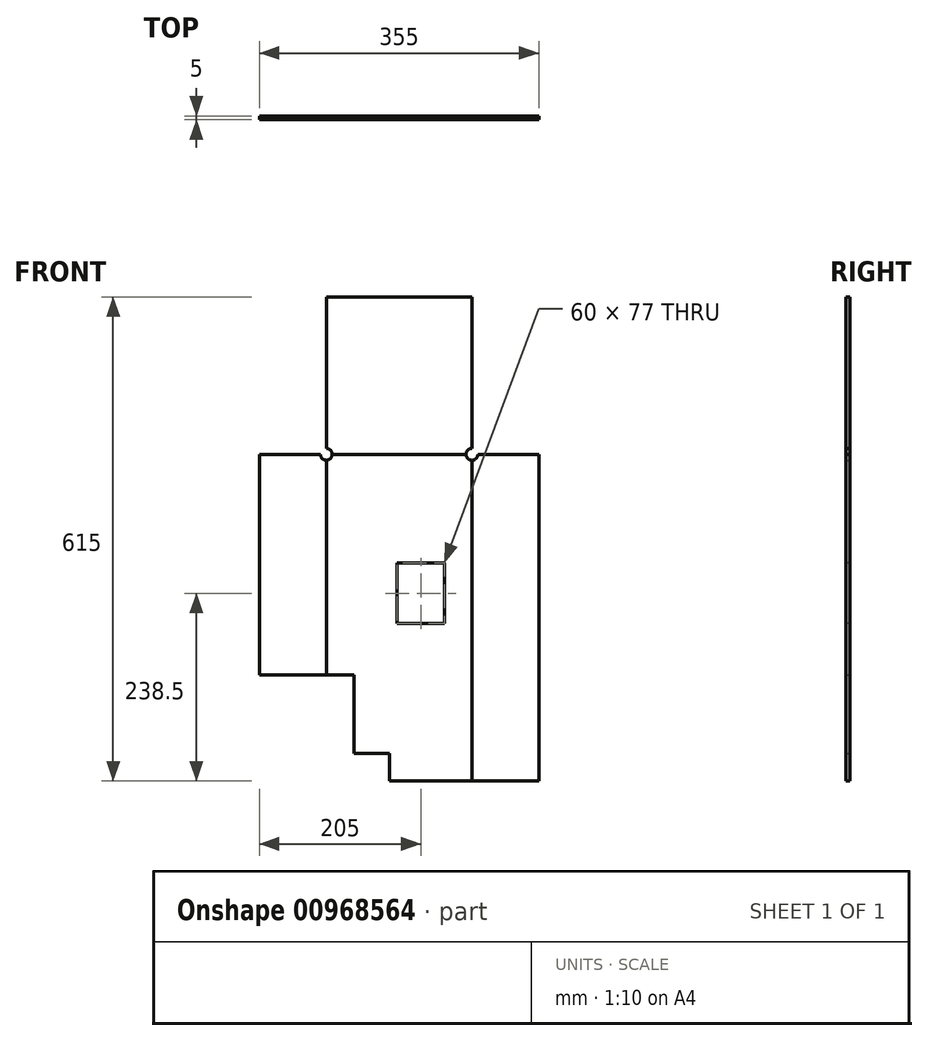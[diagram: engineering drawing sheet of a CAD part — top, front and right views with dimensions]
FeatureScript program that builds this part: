
annotation { "Feature Type Name" : "Feature", "Feature Type Description" : "" }
export const myFeature = defineFeature(function(context is Context, id is Id, definition is map)
    precondition{}
    {
        {
            var Q0;
            Q0=qCreatedBy(makeId("Front.planeOp"),FACE);
            var sketch = newSketch(context, id + "F0", { "sketchPlane" : qUnion([Q0])});
            skLineSegment(sketch, "E0.bottom", {"start": v(7.5, 0) * mm, "end": v(177.5, 0) * mm});
            skLineSegment(sketch, "E0.top", {"start": v(0, -415) * mm, "end": v(185, -415) * mm});
            skLineSegment(sketch, "E0.left", {"start": v(0, -7.5) * mm, "end": v(0, -415) * mm});
            skLineSegment(sketch, "E0.right", {"start": v(185, -7.5) * mm, "end": v(185, -415) * mm});
            skLineSegment(sketch, "E1.bottom", {"start": v(0, -415) * mm, "end": v(35, -415) * mm});
            skLineSegment(sketch, "E1.top", {"start": v(0, -280) * mm, "end": v(35, -280) * mm});
            skLineSegment(sketch, "E1.left", {"start": v(0, -415) * mm, "end": v(0, -280) * mm});
            skLineSegment(sketch, "E1.right", {"start": v(35, -415) * mm, "end": v(35, -280) * mm});
            skLineSegment(sketch, "E2.bottom", {"start": v(35, -415) * mm, "end": v(80, -415) * mm});
            skLineSegment(sketch, "E2.top", {"start": v(35, -380) * mm, "end": v(80, -380) * mm});
            skLineSegment(sketch, "E2.left", {"start": v(35, -415) * mm, "end": v(35, -380) * mm});
            skLineSegment(sketch, "E2.right", {"start": v(80, -415) * mm, "end": v(80, -380) * mm});
            skLineSegment(sketch, "E3", {"start": v(0, -415) * mm, "end": v(0, -215) * mm});
            skArc(sketch, "E4", {"start": v(0, -7.5) * mm, "mid": v(5.3, -5.3) * mm, "end": v(7.5, 0) * mm});
            skArc(sketch, "E5", {"start": v(177.5, 0) * mm, "mid": v(179.7, -5.3) * mm, "end": v(185, -7.5) * mm});
            skSolve(sketch);
        }
        {
            var Q0;
            Q0=makeQuery(id+"F0.imprint","IMPRINT",FACE,{"disambiguationData":[TD([[makeQuery(id+"F0.imprint","IMPRINT",EDGE,{"derivedFrom":sQuery(id+"F0.wireOp",EDGE,"E0.bottom")}),-1.0]])]});
            extrude(context, id + "F1", {"entities" : qUnion([Q0]), "depth" : 5 * mm, "offsetDistance" : 25 * mm});
        }
        {
            var Q0;
            Q0=qCreatedBy(makeId("Front.planeOp"),FACE);
            var sketch = newSketch(context, id + "F2", { "sketchPlane" : qUnion([Q0])});
            skLineSegment(sketch, "E6", {"start": v(0, 0) * mm, "end": v(90, 0) * mm});
            skLineSegment(sketch, "E7", {"start": v(90, 0) * mm, "end": v(90, -215) * mm});
            skLineSegment(sketch, "E8.bottom", {"start": v(90, -215) * mm, "end": v(150, -215) * mm});
            skLineSegment(sketch, "E8.top", {"start": v(90, -138) * mm, "end": v(150, -138) * mm});
            skLineSegment(sketch, "E8.left", {"start": v(90, -215) * mm, "end": v(90, -138) * mm});
            skLineSegment(sketch, "E8.right", {"start": v(150, -215) * mm, "end": v(150, -138) * mm});
            skSolve(sketch);
        }
        {
            var Q0;
            Q0=qSketchRegion(id+"F2",true);
            extrude(context, id + "F3", {"entities" : qUnion([Q0]), "operationType" : NewBodyOperationType.REMOVE, "oppositeDirection" : true, "depth" : 25 * mm, "offsetDistance" : 25 * mm, "hasSecondDirection" : true, "secondDirectionOppositeDirection" : false, "secondDirectionDepth" : 25 * mm});
        }
        {
            var Q0;
            Q0=qCreatedBy(makeId("Front.planeOp"),FACE);
            var sketch = newSketch(context, id + "F4", { "sketchPlane" : qUnion([Q0])});
            skLineSegment(sketch, "E9", {"start": v(-7.5, 0) * mm, "end": v(-85, 0) * mm});
            skLineSegment(sketch, "E10", {"start": v(-85, 0) * mm, "end": v(-85, -280) * mm});
            skLineSegment(sketch, "E11", {"start": v(-85, -280) * mm, "end": v(0, -280) * mm});
            skLineSegment(sketch, "E12", {"start": v(0, -280) * mm, "end": v(0, -7.5) * mm});
            skArc(sketch, "E13", {"start": v(-7.5, 0) * mm, "mid": v(5.3, -5.3) * mm, "end": v(0, 7.5) * mm});
            skLineSegment(sketch, "E14", {"start": v(7.5, 0) * mm, "end": v(177.5, 0) * mm});
            skArc(sketch, "E15", {"start": v(185, 7.5) * mm, "mid": v(179.7, -5.3) * mm, "end": v(192.5, 0) * mm});
            skLineSegment(sketch, "E16", {"start": v(192.5, 0) * mm, "end": v(270, 0) * mm});
            skLineSegment(sketch, "E17", {"start": v(270, 0) * mm, "end": v(270, -415) * mm});
            skLineSegment(sketch, "E18", {"start": v(270, -415) * mm, "end": v(185, -415) * mm});
            skLineSegment(sketch, "E19", {"start": v(185, -415) * mm, "end": v(185, -7.5) * mm});
            skLineSegment(sketch, "E20", {"start": v(185, 7.5) * mm, "end": v(185, 200) * mm});
            skLineSegment(sketch, "E21", {"start": v(185, 200) * mm, "end": v(0, 200) * mm});
            skLineSegment(sketch, "E22", {"start": v(0, 200) * mm, "end": v(0, 7.5) * mm});
            skSolve(sketch);
        }
        {
            var Q0;
            Q0 = qSketchRegion(id + "F4", true);
            extrude(context, id + "F5", {"entities" : qUnion([Q0]), "depth" : 5 * mm, "offsetDistance" : 25 * mm});
        }
    });
